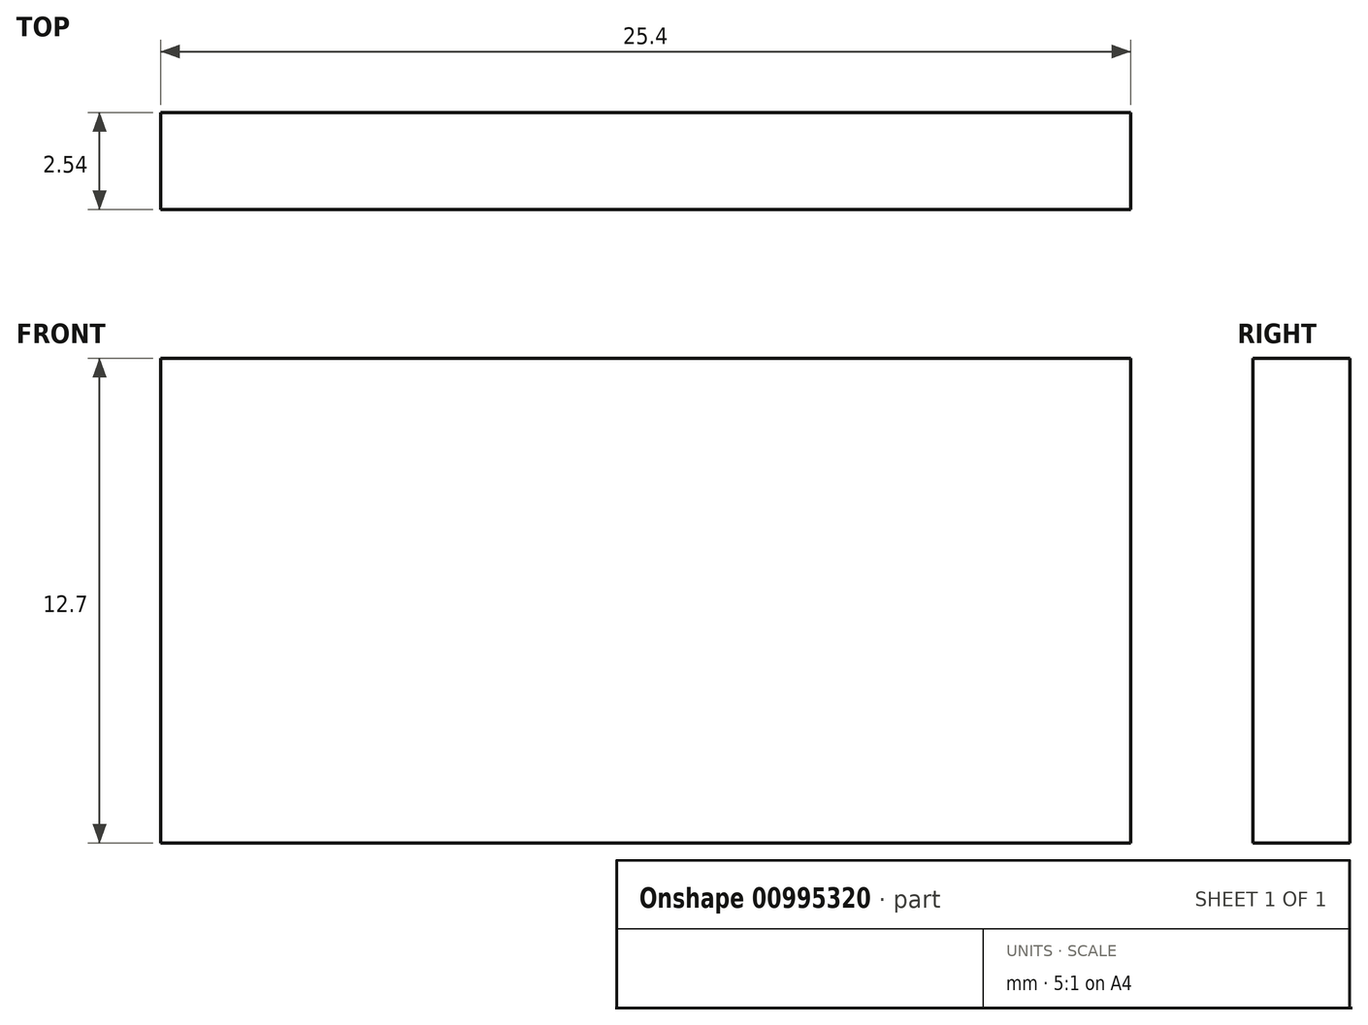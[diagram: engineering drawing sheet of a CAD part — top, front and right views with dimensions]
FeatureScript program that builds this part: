
annotation { "Feature Type Name" : "Feature", "Feature Type Description" : "" }
export const myFeature = defineFeature(function(context is Context, id is Id, definition is map)
    precondition{}
    {
        {
            var Q0;
            Q0=qCreatedBy(makeId("Front.planeOp"),FACE);
            var sketch = newSketch(context, id + "F0", { "sketchPlane" : qUnion([Q0])});
            skLineSegment(sketch, "E0.bottom", {"start": v(0, 0) * mm, "end": v(25.4, 0) * mm});
            skLineSegment(sketch, "E0.top", {"start": v(0, 12.7) * mm, "end": v(25.4, 12.7) * mm});
            skLineSegment(sketch, "E0.left", {"start": v(0, 0) * mm, "end": v(0, 12.7) * mm});
            skLineSegment(sketch, "E0.right", {"start": v(25.4, 0) * mm, "end": v(25.4, 12.7) * mm});
            skSolve(sketch);
        }
        {
            var Q0;
            Q0 = qSketchRegion(id + "F0", true);
            extrude(context, id + "F1", {"entities" : qUnion([Q0]), "depth" : 2.54 * mm, "offsetDistance" : 25.4 * mm});
        }
    });
